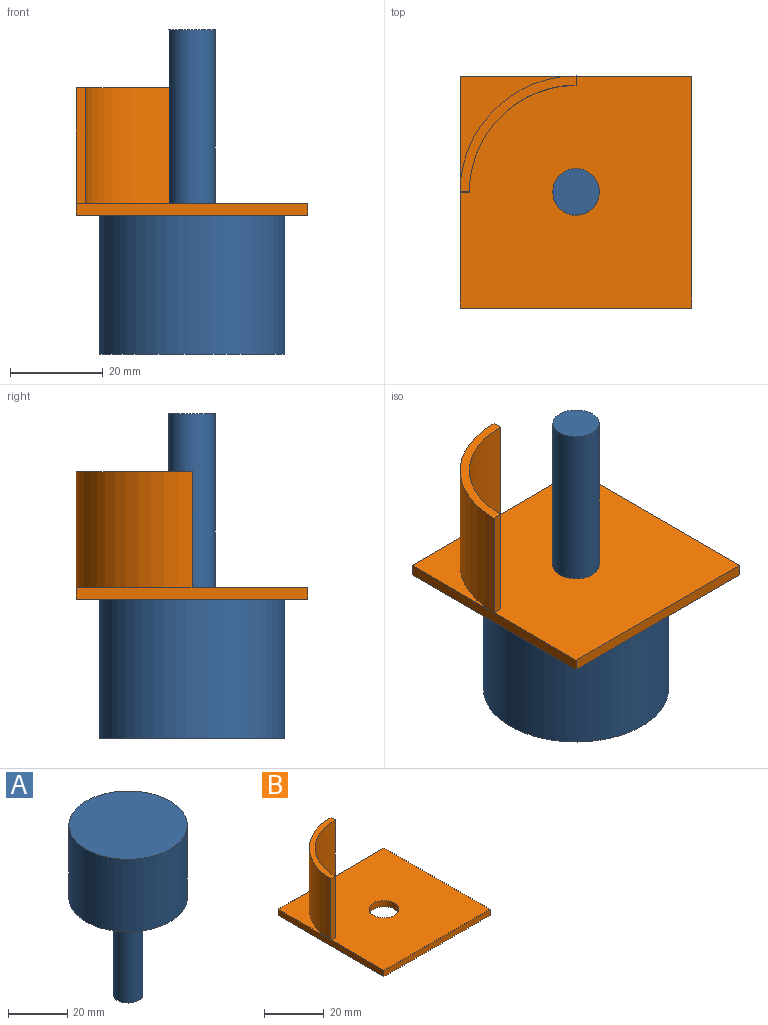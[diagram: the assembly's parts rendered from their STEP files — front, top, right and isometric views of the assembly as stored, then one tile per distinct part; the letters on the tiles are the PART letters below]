
ASSEMBLY  parts=2 mates=1
PART A: 5 faces, bbox 40x40x70 mm
  f0: cylinder r=5mm len=40mm, axis (0,0,-1), area 1256.6mm2, adj f1,f4
  f1: plane 10x10mm, normal (0,0,-1), area 78.5mm2, adj f0
  f2: cylinder r=20mm len=40mm, axis (0,0,-1), area 3769.9mm2, adj f3,f4
  f3: plane 40x40mm, normal (0,0,1), area 1256.6mm2, adj f2
  f4: plane 40x40mm, normal (0,0,-1), area 1178.1mm2, adj f0,f2
PART B: 13 faces, bbox 50x50x27.5 mm
  f0: plane 50x50mm, normal (0,0,1), area 2211.9mm2, adj f1,f2,f3,f4,f5,f8,f9,f11
  f1: plane 50x2.5mm, normal (0,1,0), area 125mm2, adj f0,f2,f5,f6,f7
  f2: plane 50x2.5mm, normal (-1,0,0), area 125mm2, adj f0,f1,f3,f6,f7
  f3: plane 50x2.5mm, normal (0,-1,0), area 125mm2, adj f0,f2,f5,f7
  f4: cylinder r=5mm len=10mm, axis (0,0,-1), area 78.5mm2, adj f0,f7
  f5: plane 50x2.5mm, normal (1,0,0), area 125mm2, adj f0,f1,f3,f7
  f6: plane 25x25mm, normal (0,0,1), area 134.1mm2, adj f1,f2,f10
  f7: plane 50x50mm, normal (0,0,-1), area 2421.5mm2, adj f1,f2,f3,f4,f5
  f8: cylinder r=23mm len=25mm, axis (0,0,-1), area 903.2mm2, adj f0,f9,f11,f12
  f9: plane 25x2mm, normal (1,0,0), area 50mm2, adj f0,f8,f10,f12
  f10: cylinder r=25mm len=25mm, axis (0,0,-1), area 981.7mm2, adj f6,f9,f11,f12
  f11: plane 25x2mm, normal (0,-1,0), area 50mm2, adj f0,f8,f10,f12
  f12: plane 25x25mm, normal (0,0,1), area 75.4mm2, adj f8,f9,f10,f11
PLACE A rot(axis=(1,0,0),180deg) t=(-335.23,109.64,34.86)mm
PLACE B t=(9.79,10.56,-5.14)mm
MATE cylindrical A.f0 <-> B.f4  axis (0,0,1) through (9.79,10.56,-5.14)mm
